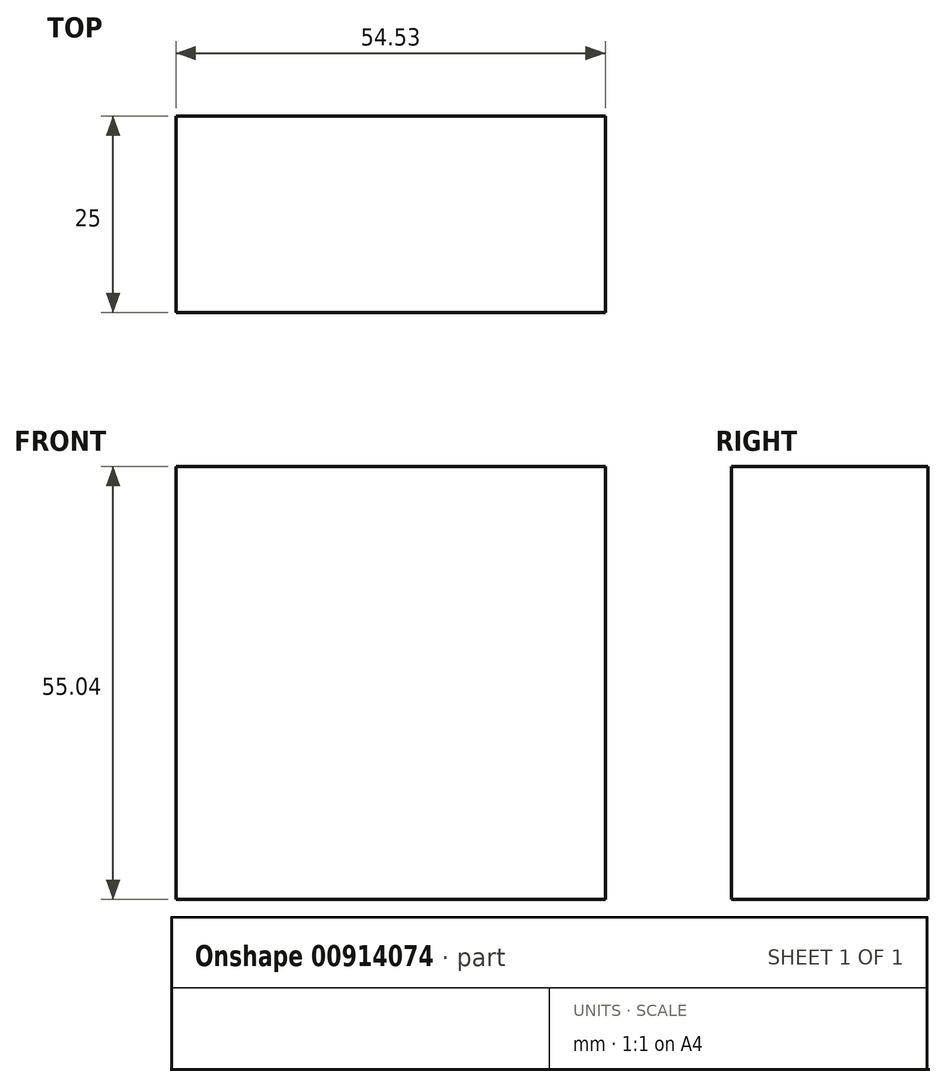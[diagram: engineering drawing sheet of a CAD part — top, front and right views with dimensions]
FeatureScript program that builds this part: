
annotation { "Feature Type Name" : "Feature", "Feature Type Description" : "" }
export const myFeature = defineFeature(function(context is Context, id is Id, definition is map)
    precondition{}
    {
        {
            var Q0;
            Q0=qCreatedBy(makeId("Front.planeOp"),FACE);
            var sketch = newSketch(context, id + "F0", { "sketchPlane" : qUnion([Q0])});
            skLineSegment(sketch, "E0.bottom", {"start": v(-120.25, 0) * mm, "end": v(-65.72, 0) * mm});
            skLineSegment(sketch, "E0.top", {"start": v(-120.25, 55.04) * mm, "end": v(-65.72, 55.04) * mm});
            skLineSegment(sketch, "E0.left", {"start": v(-120.25, 0) * mm, "end": v(-120.25, 55.04) * mm});
            skLineSegment(sketch, "E0.right", {"start": v(-65.72, 0) * mm, "end": v(-65.72, 55.04) * mm});
            skPoint(sketch, "E0.middle", {"position": v(-92.99, 27.52) * mm});
            skSolve(sketch);
        }
        {
            var Q0;
            Q0=makeQuery(id+"F0.imprint","IMPRINT",FACE,{"disambiguationData":[TD([[makeQuery(id+"F0.imprint","IMPRINT",EDGE,{"derivedFrom":sQuery(id+"F0.wireOp",EDGE,"E0.bottom")}),1.0]])]});
            extrude(context, id + "F1", {"entities" : qUnion([Q0]), "depth" : 25 * mm, "offsetDistance" : 25 * mm});
        }
    });
